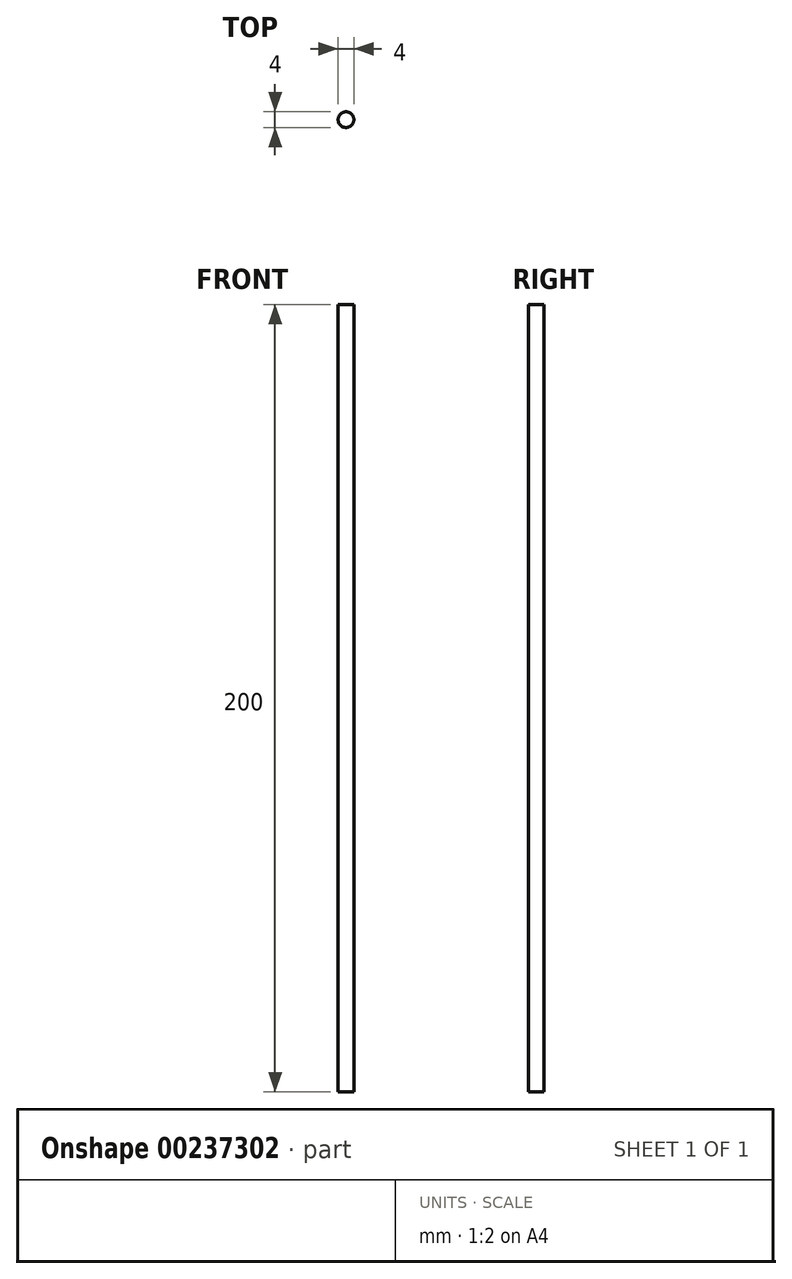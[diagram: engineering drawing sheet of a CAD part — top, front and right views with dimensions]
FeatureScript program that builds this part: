
annotation { "Feature Type Name" : "Feature", "Feature Type Description" : "" }
export const myFeature = defineFeature(function(context is Context, id is Id, definition is map)
    precondition{}
    {
        {
            var Q0;
            Q0=qCreatedBy(makeId("Top.planeOp"),FACE);
            var sketch = newSketch(context, id + "F0", { "sketchPlane" : qUnion([Q0])});
            skCircle(sketch, "E0", {"center": v(0, 0) * mm, "radius": 2 * mm});
            skSolve(sketch);
        }
        {
            var Q0;
            Q0=makeQuery(id+"F0.imprint","IMPRINT",FACE,{"disambiguationData":[TD([[makeQuery(id+"F0.imprint","IMPRINT",EDGE,{"derivedFrom":sQuery(id+"F0.wireOp",EDGE,"E0")}),1.0]])]});
            extrude(context, id + "F1", {"entities" : qUnion([Q0]), "depth" : 200 * mm});
        }
    });
